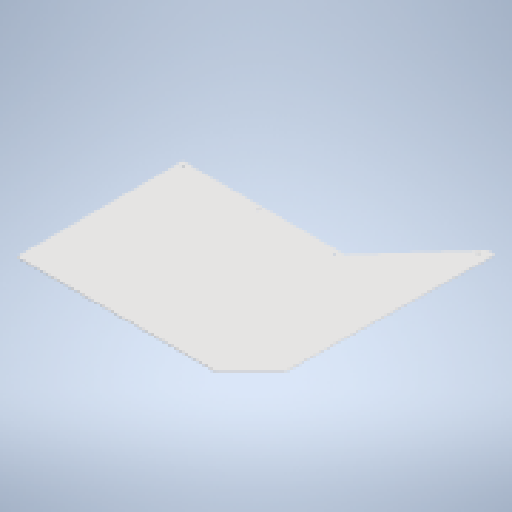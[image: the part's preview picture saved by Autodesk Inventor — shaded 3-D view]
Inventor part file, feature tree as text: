
AUTODESK INVENTOR PART (.ipt)
format: ipt  version: 2025 (Build 290162010, 162A)  size: 332,800 bytes
history: native  units: mm
features: other x3, sketch x3, extrude x2, projected_geometry x2, sheet_metal_op x1, pattern_linear x1
ambient origin geometry x8: Origin, YZ Plane, XZ Plane, XY Plane, X Axis, Y Axis, Z Axis, Center Point
bodies: Body1 (feature_tree)
feature tree (12):
  sheet_metal_op  "Face2"
  other  "Corner Chamfer1"
  extrude  "Extrusion2"  Depth=700.0mm
  pattern_linear  "Rectangular Pattern2"  Spacing1=108.495mm  [1 undecoded]
  extrude  "Extrusion3"  Depth=10.0mm
  sketch  "Sketch8"  dims[d43=1200.0mm d44=2897.0mm d45=53.0mm d46=947.0mm d47=150.0mm d48=103.0mm d49=700.0mm]
  other  "Plate4"
  sketch  "Sketch9"  dims[d50=3.0mm]
  projected_geometry  "Projected Loop2"
  sketch  "Sketch10"  dims[d51=6.0mm d52=6.0mm d53=45.0deg d54=108.495mm d55=306.0mm d57=110.253mm d61=8.37758mm d65=10.0mm d66=30.0mm d67=11.0mm d68=20.0mm d69=20.0mm d70=0.0mm d71=0.0mm d72=30.0mm d74=320.0mm d75=15.0mm d76=30.0mm d77=0.0mm d78=0.0mm]
  projected_geometry  "Projected Loop3"
  other  "Definition1"
note: 1 required parameter value undecoded (feature->parameter linkage not recoverable at this tier; creation-order binding heuristic only, values carry confidence <= 0.55)
